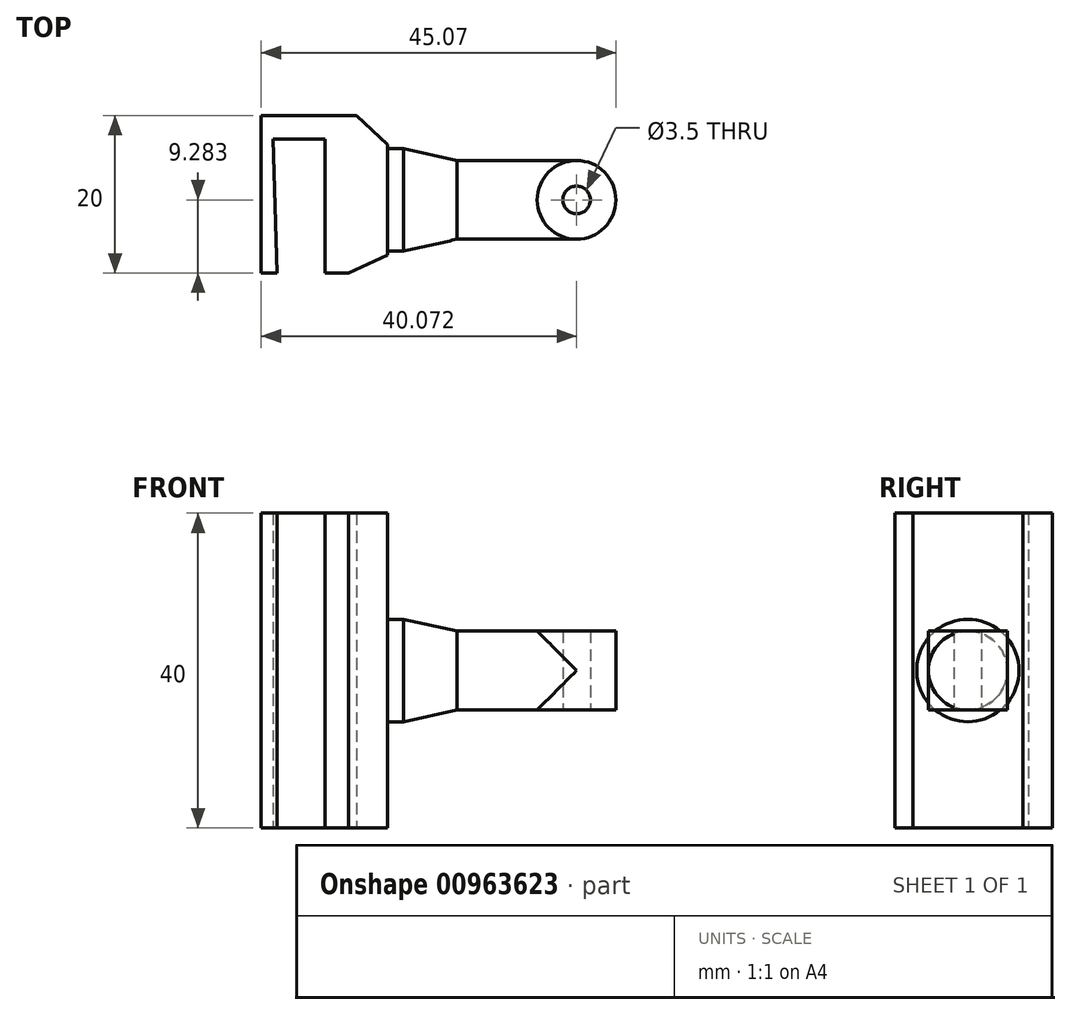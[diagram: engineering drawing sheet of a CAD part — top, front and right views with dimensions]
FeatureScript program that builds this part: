
annotation { "Feature Type Name" : "Feature", "Feature Type Description" : "" }
export const myFeature = defineFeature(function(context is Context, id is Id, definition is map)
    precondition{}
    {
        {
            var Q0;
            Q0=qCreatedBy(makeId("Top.planeOp"),FACE);
            var sketch = newSketch(context, id + "F0", { "sketchPlane" : qUnion([Q0])});
            skLineSegment(sketch, "E0", {"start": v(-33.94, -23.13) * mm, "end": v(-33.94, -3.13) * mm});
            skLineSegment(sketch, "E1", {"start": v(-33.94, -23.13) * mm, "end": v(-31.94, -23.13) * mm});
            skLineSegment(sketch, "E2", {"start": v(-31.94, -23.13) * mm, "end": v(-32.44, -6.13) * mm});
            skLineSegment(sketch, "E3", {"start": v(-33.94, -3.13) * mm, "end": v(-21.84, -3.13) * mm});
            skLineSegment(sketch, "E4", {"start": v(-25.84, -23.13) * mm, "end": v(-22.84, -23.13) * mm});
            skLineSegment(sketch, "E5", {"start": v(-25.84, -23.13) * mm, "end": v(-25.84, -6.13) * mm});
            skLineSegment(sketch, "E6", {"start": v(-25.84, -6.13) * mm, "end": v(-32.44, -6.13) * mm});
            skLineSegment(sketch, "E7", {"start": v(-21.84, -3.13) * mm, "end": v(-17.87, -6.85) * mm});
            skLineSegment(sketch, "E8", {"start": v(-17.87, -6.85) * mm, "end": v(-17.87, -20.85) * mm});
            skLineSegment(sketch, "E9", {"start": v(-17.87, -20.85) * mm, "end": v(-22.84, -23.13) * mm});
            skLineSegment(sketch, "E10", {"start": v(-17.87, -20.35) * mm, "end": v(-15.87, -20.35) * mm});
            skLineSegment(sketch, "E11", {"start": v(-15.87, -20.35) * mm, "end": v(-15.87, -7.35) * mm});
            skLineSegment(sketch, "E12", {"start": v(-15.87, -7.35) * mm, "end": v(-17.87, -7.35) * mm});
            skLineSegment(sketch, "E13", {"start": v(-17.87, -13.85) * mm, "end": v(-15.87, -13.85) * mm});
            skLineSegment(sketch, "E14", {"start": v(-15.87, -13.85) * mm, "end": v(6.13, -13.85) * mm});
            skLineSegment(sketch, "E15", {"start": v(-15.87, -7.35) * mm, "end": v(-9.07, -8.85) * mm});
            skCircle(sketch, "E16", {"center": v(6.13, -13.85) * mm, "radius": 5 * mm});
            skCircle(sketch, "E17", {"center": v(6.13, -13.85) * mm, "radius": 1.75 * mm});
            skLineSegment(sketch, "E18", {"start": v(-9.07, -13.85) * mm, "end": v(-9.07, -8.85) * mm});
            skLineSegment(sketch, "E19", {"start": v(-9.07, -13.85) * mm, "end": v(-9.07, -18.85) * mm});
            skLineSegment(sketch, "E20", {"start": v(-15.87, -20.35) * mm, "end": v(-9.07, -18.85) * mm});
            skLineSegment(sketch, "E21", {"start": v(-9.07, -8.85) * mm, "end": v(6.13, -8.85) * mm});
            skLineSegment(sketch, "E22", {"start": v(6.13, -8.85) * mm, "end": v(6.13, -18.85) * mm});
            skLineSegment(sketch, "E23", {"start": v(6.13, -18.85) * mm, "end": v(-9.07, -18.85) * mm});
            skSolve(sketch);
        }
        {
            var Q0;
            Q0=makeQuery(id+"F0.imprint","IMPRINT",FACE,{"disambiguationData":[TD([[makeQuery(id+"F0.imprint","IMPRINT",EDGE,{"derivedFrom":sQuery(id+"F0.wireOp",EDGE,"E0")}),-1.0]])]});
            extrude(context, id + "F1", {"entities" : qUnion([Q0]), "endBound" : BoundingType.SYMMETRIC, "depth" : 40 * mm, "offsetDistance" : 25 * mm});
        }
        {
            var Q0;
            {var subQ0=sQuery(id+"F0.wireOp",EDGE,"E12");Q0=makeQuery(id+"F0.imprint","IMPRINT",FACE,{"disambiguationData":[TD([[makeQuery(id+"F0.imprint","IMPRINT",EDGE,{"derivedFrom":subQ0}),1.0]])]});}
            var Q1;
            Q1=sQuery(id+"F0.wireOp",EDGE,"E13");
            revolve(context, id + "F2", {"operationType" : NewBodyOperationType.ADD, "surfaceOperationType" : NewSurfaceOperationType.NEW, "entities" : qUnion([Q0]), "axis" : qUnion([Q1]), "revolveType" : RevolveType.FULL});
        }
        {
            var Q0;
            {var subQ0=sQuery(id+"F0.wireOp",EDGE,"E15");Q0=makeQuery(id+"F0.imprint","IMPRINT",FACE,{"disambiguationData":[TD([[makeQuery(id+"F0.imprint","IMPRINT",EDGE,{"derivedFrom":subQ0}),-1.0]])]});}
            var Q1;
            Q1=sQuery(id+"F0.wireOp",EDGE,"E14");
            revolve(context, id + "F3", {"operationType" : NewBodyOperationType.ADD, "surfaceOperationType" : NewSurfaceOperationType.NEW, "entities" : qUnion([Q0]), "axis" : qUnion([Q1]), "revolveType" : RevolveType.FULL});
        }
        {
            var Q0;
            {var subQ0=sQuery(id+"F0.wireOp",EDGE,"E18");Q0=makeQuery(id+"F0.imprint","IMPRINT",FACE,{"disambiguationData":[TD([[makeQuery(id+"F0.imprint","IMPRINT",EDGE,{"derivedFrom":subQ0}),-1.0]])]});}
            var Q1;
            {var subQ0=sQuery(id+"F0.wireOp",EDGE,"E16");var subQ1=sQuery(id+"F0.wireOp",EDGE,"E14");var subQ2=makeQuery(id+"F0.imprint","INTERSECT",VERTEX,{"derivedFrom":[subQ1,subQ0]});Q1=makeQuery(id+"F0.imprint","IMPRINT",FACE,{"disambiguationData":[TD([[makeQuery(id+"F0.imprint","IMPRINT",EDGE,{"disambiguationData":[TD([[subQ2,-1.0]])],"derivedFrom":subQ1}),1.0]])]});}
            var Q2;
            {var subQ0=sQuery(id+"F0.wireOp",EDGE,"E22");var subQ1=sQuery(id+"F0.wireOp",EDGE,"E14");var subQ2=makeQuery(id+"F0.imprint","INTERSECT",VERTEX,{"derivedFrom":[subQ1,subQ0]});Q2=makeQuery(id+"F0.imprint","IMPRINT",FACE,{"disambiguationData":[TD([[makeQuery(id+"F0.imprint","IMPRINT",EDGE,{"disambiguationData":[TD([[subQ2,1.0]])],"derivedFrom":subQ1}),1.0]])]});}
            var Q3;
            Q3=sQuery(id+"F0.wireOp",EDGE,"E14");
            revolve(context, id + "F4", {"operationType" : NewBodyOperationType.ADD, "surfaceOperationType" : NewSurfaceOperationType.NEW, "entities" : qUnion([Q0, Q1, Q2]), "axis" : qUnion([Q3]), "revolveType" : RevolveType.FULL});
        }
        {
            var Q0;
            {var subQ0=sQuery(id+"F0.wireOp",EDGE,"E22");var subQ1=sQuery(id+"F0.wireOp",EDGE,"E14");var subQ2=makeQuery(id+"F0.imprint","INTERSECT",VERTEX,{"derivedFrom":[subQ1,subQ0]});Q0=makeQuery(id+"F0.imprint","IMPRINT",FACE,{"disambiguationData":[TD([[makeQuery(id+"F0.imprint","IMPRINT",EDGE,{"disambiguationData":[TD([[subQ2,1.0]])],"derivedFrom":subQ1}),-1.0]])]});}
            var Q1;
            {var subQ0=sQuery(id+"F0.wireOp",EDGE,"E22");var subQ1=sQuery(id+"F0.wireOp",EDGE,"E17");var subQ2=makeQuery(id+"F0.imprint","INTERSECT",VERTEX,{"disambiguationData":[OD(0.0)],"derivedFrom":[subQ1,subQ0]});Q1=makeQuery(id+"F0.imprint","IMPRINT",FACE,{"disambiguationData":[TD([[makeQuery(id+"F0.imprint","IMPRINT",EDGE,{"disambiguationData":[TD([[subQ2,1.0]])],"derivedFrom":subQ1}),1.0]])]});}
            var Q2;
            {var subQ0=sQuery(id+"F0.wireOp",EDGE,"E22");var subQ1=sQuery(id+"F0.wireOp",EDGE,"E14");var subQ2=makeQuery(id+"F0.imprint","INTERSECT",VERTEX,{"derivedFrom":[subQ1,subQ0]});Q2=makeQuery(id+"F0.imprint","IMPRINT",FACE,{"disambiguationData":[TD([[makeQuery(id+"F0.imprint","IMPRINT",EDGE,{"disambiguationData":[TD([[subQ2,1.0]])],"derivedFrom":subQ1}),1.0]])]});}
            extrude(context, id + "F5", {"entities" : qUnion([Q0, Q1, Q2]), "operationType" : NewBodyOperationType.REMOVE, "endBound" : BoundingType.SYMMETRIC, "depth" : 10 * mm, "offsetDistance" : 25 * mm});
        }
        {
            var Q0;
            {var subQ0=sQuery(id+"F0.wireOp",EDGE,"E16");var subQ1=sQuery(id+"F0.wireOp",EDGE,"E14");var subQ2=makeQuery(id+"F0.imprint","INTERSECT",VERTEX,{"derivedFrom":[subQ1,subQ0]});Q0=makeQuery(id+"F0.imprint","IMPRINT",FACE,{"disambiguationData":[TD([[makeQuery(id+"F0.imprint","IMPRINT",EDGE,{"disambiguationData":[TD([[subQ2,-1.0]])],"derivedFrom":subQ1}),1.0]])]});}
            var Q1;
            {var subQ0=sQuery(id+"F0.wireOp",EDGE,"E16");var subQ1=sQuery(id+"F0.wireOp",EDGE,"E14");var subQ2=makeQuery(id+"F0.imprint","INTERSECT",VERTEX,{"derivedFrom":[subQ1,subQ0]});Q1=makeQuery(id+"F0.imprint","IMPRINT",FACE,{"disambiguationData":[TD([[makeQuery(id+"F0.imprint","IMPRINT",EDGE,{"disambiguationData":[TD([[subQ2,-1.0]])],"derivedFrom":subQ1}),-1.0]])]});}
            var Q2;
            {var subQ0=sQuery(id+"F0.wireOp",EDGE,"E22");var subQ4=sQuery(id+"F0.wireOp",EDGE,"E17");var subQ5=makeQuery(id+"F0.imprint","INTERSECT",VERTEX,{"disambiguationData":[OD(0.0)],"derivedFrom":[subQ4,subQ0]});Q2=makeQuery(id+"F0.imprint","IMPRINT",FACE,{"disambiguationData":[TD([[makeQuery(id+"F0.imprint","IMPRINT",EDGE,{"disambiguationData":[TD([[subQ5,1.0]])],"derivedFrom":subQ4}),-1.0]])]});}
            extrude(context, id + "F6", {"entities" : qUnion([Q0, Q1, Q2]), "operationType" : NewBodyOperationType.ADD, "endBound" : BoundingType.SYMMETRIC, "depth" : 10 * mm, "offsetDistance" : 25 * mm});
        }
    });
